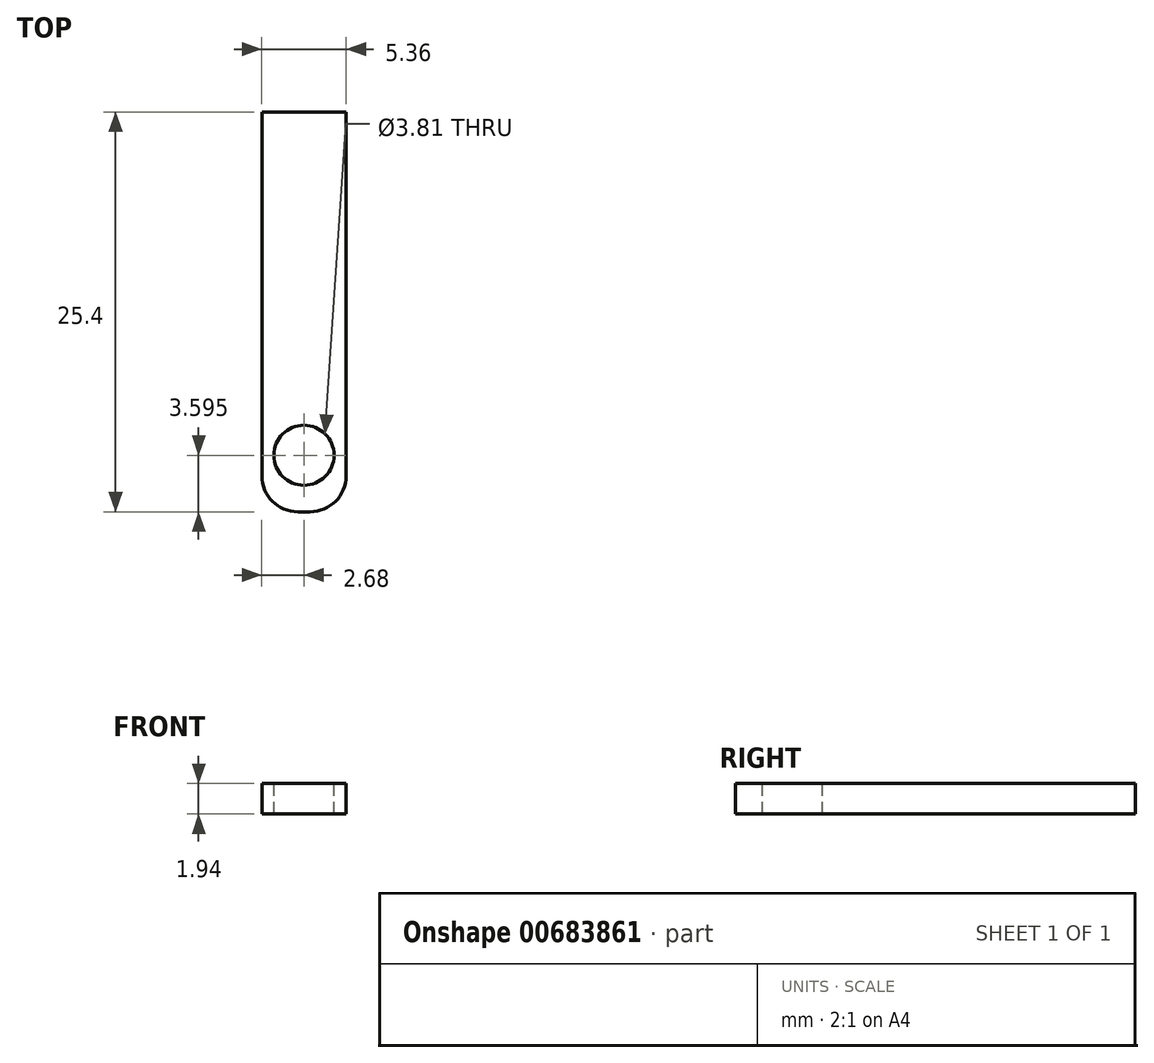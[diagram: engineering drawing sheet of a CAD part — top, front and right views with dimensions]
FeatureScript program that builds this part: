
annotation { "Feature Type Name" : "Feature", "Feature Type Description" : "" }
export const myFeature = defineFeature(function(context is Context, id is Id, definition is map)
    precondition{}
    {
        {
            var Q0;
            Q0=qCreatedBy(makeId("Front.planeOp"),FACE);
            var sketch = newSketch(context, id + "F0", { "sketchPlane" : qUnion([Q0])});
            skLineSegment(sketch, "E0.bottom", {"start": v(2.68, -0.97) * mm, "end": v(-2.68, -0.97) * mm});
            skLineSegment(sketch, "E0.top", {"start": v(2.68, 0.97) * mm, "end": v(-2.68, 0.97) * mm});
            skLineSegment(sketch, "E0.left", {"start": v(2.68, -0.97) * mm, "end": v(2.68, 0.97) * mm});
            skLineSegment(sketch, "E0.right", {"start": v(-2.68, -0.97) * mm, "end": v(-2.68, 0.97) * mm});
            skPoint(sketch, "E0.middle", {"position": v(0, 0) * mm});
            skSolve(sketch);
        }
        {
            var Q0;
            Q0=makeQuery(id+"F0.imprint","IMPRINT",FACE,{"disambiguationData":[TD([[makeQuery(id+"F0.imprint","IMPRINT",EDGE,{"derivedFrom":sQuery(id+"F0.wireOp",EDGE,"E0.bottom")}),-1.0]])]});
            extrude(context, id + "F1", {"entities" : qUnion([Q0]), "depth" : 25.4 * mm, "offsetDistance" : 25.4 * mm});
        }
        {
            var Q0;
            Q0=makeQuery(id+"F1.opExtrude","CAP_EDGE",EDGE,{"disambiguationData":[OSD([sQuery(id+"F0.wireOp",EDGE,"E0.right")])],"isStart":false});
            var Q1;
            Q1=makeQuery(id+"F1.opExtrude","CAP_EDGE",EDGE,{"disambiguationData":[OSD([sQuery(id+"F0.wireOp",EDGE,"E0.left")])],"isStart":false});
            fillet(context, id + "F2", {"entities" : qUnion([Q0, Q1]), "radius" : 2.3 * mm, "tangentPropagation" : true, "allowEdgeOverflow" : false});
        }
        {
            var Q0;
            Q0=makeQuery(id+"F1.opExtrude","SWEPT_FACE",FACE,{"disambiguationData":[OSD([sQuery(id+"F0.wireOp",EDGE,"E0.top")])]});
            var sketch = newSketch(context, id + "F3", { "sketchPlane" : qUnion([Q0])});
            skCircle(sketch, "E1", {"center": v(0, -21.8) * mm, "radius": 1.9 * mm});
            skSolve(sketch);
        }
        {
            var Q0;
            Q0=makeQuery(id+"F3.imprint","IMPRINT",FACE,{"disambiguationData":[TD([[makeQuery(id+"F3.imprint","IMPRINT",EDGE,{"derivedFrom":sQuery(id+"F3.wireOp",EDGE,"E1")}),1.0]])]});
            extrude(context, id + "F4", {"entities" : qUnion([Q0]), "operationType" : NewBodyOperationType.REMOVE, "oppositeDirection" : true, "depth" : 2.4 * mm, "offsetDistance" : 25.4 * mm});
        }
    });
